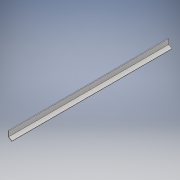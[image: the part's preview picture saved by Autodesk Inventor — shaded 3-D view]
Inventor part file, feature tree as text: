
AUTODESK INVENTOR PART (.ipt)
format: ipt  version: 2018 (Build 220112000, 112)  size: 100,864 bytes
history: native  units: mm
features: other x1, extrude x1, sketch x1
ambient origin geometry x8: Origin, YZ Plane, XZ Plane, XY Plane, X Axis, Y Axis, Z Axis, Center Point
bodies: Body1 (feature_tree)
feature tree (3):
  other  "ソリッド1"
  extrude  "押し出し1"  Depth=7.0mm
  sketch  "スケッチ1"
